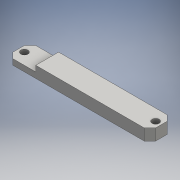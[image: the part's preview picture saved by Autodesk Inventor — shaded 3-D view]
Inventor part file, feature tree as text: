
AUTODESK INVENTOR PART (.ipt)
format: ipt  version: 2016 (Build 200138000, 138)  size: 126,976 bytes
history: native  units: mm
features: extrude x4, chamfer x4, sketch x4, other x1
ambient origin geometry x8: Origin, YZ Plane, XZ Plane, XY Plane, X Axis, Y Axis, Z Axis, Center Point
bodies: Body1 (feature_tree)
feature tree (13):
  other  "ソリッド1"
  extrude  "押し出し1"  Depth=50.0mm
  extrude  "押し出し2"  Depth=4.0mm
  chamfer  "面取り1"  Distance=8.0mm
  chamfer  "面取り2"  Distance=2.5mm
  extrude  "押し出し3"  Depth=2.0mm
  chamfer  "面取り3"  Distance=5.0mm
  chamfer  "面取り4"  Distance=2.0mm Angle=45.0deg
  extrude  "押し出し4"  Depth=2.0mm TaperAngle=45.0deg
  sketch  "スケッチ1"
  sketch  "スケッチ2"
  sketch  "スケッチ3"
  sketch  "スケッチ4"
